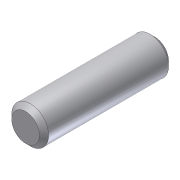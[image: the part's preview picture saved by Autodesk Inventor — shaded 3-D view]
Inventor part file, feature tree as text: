
AUTODESK INVENTOR PART (.ipt)
format: ipt  version: unknown  size: 163,840 bytes
history: native  units: mm (DEFAULTED — no unit token found)
features: extrude x1, chamfer x1, sketch x1
ambient origin geometry x8: Origin, YZ Plane, XZ Plane, XY Plane, X Axis, Y Axis, Z Axis, Center Point
feature tree (3):
  extrude  "Extrusion1"  Depth=22.225mm TaperAngle=0.0deg
  chamfer  "Chamfer1"  Distance=0.7874mm
  sketch  "Sketch1"  dims[d0=6.35mm d1=22.225mm d2=0.0mm d3=0.7874mm d4=3.175mm d5=45.0deg]
